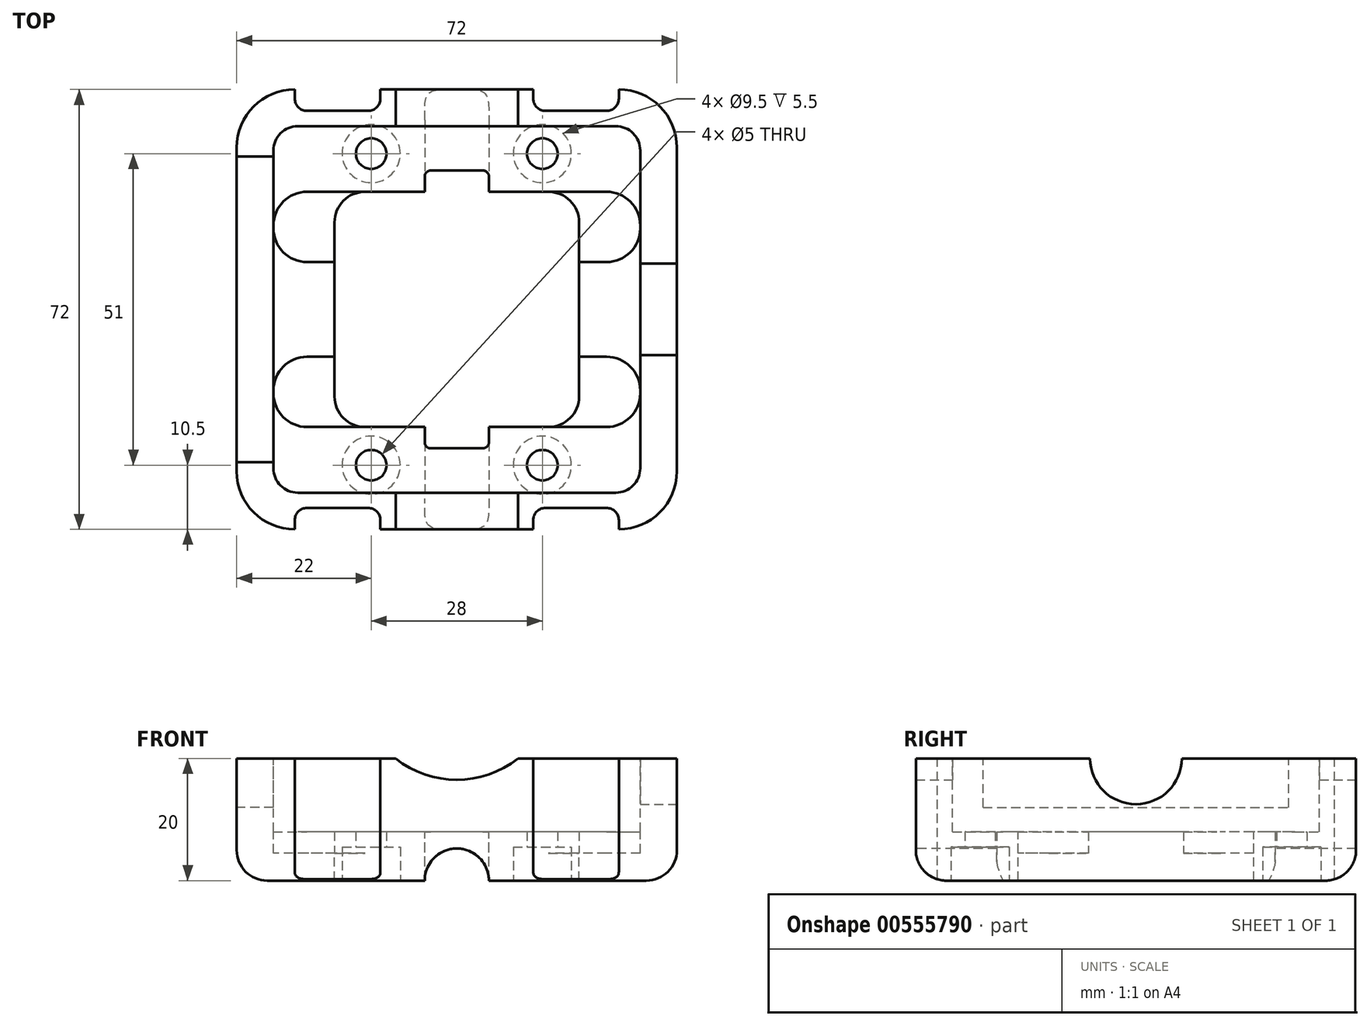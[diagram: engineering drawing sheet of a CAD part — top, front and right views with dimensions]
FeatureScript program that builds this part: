
annotation { "Feature Type Name" : "Feature", "Feature Type Description" : "" }
export const myFeature = defineFeature(function(context is Context, id is Id, definition is map)
    precondition{}
    {
        {
            var Q0;
            Q0=qCreatedBy(makeId("Top.planeOp"),FACE);
            var sketch = newSketch(context, id + "F0", { "sketchPlane" : qUnion([Q0])});
            skLineSegment(sketch, "E0.bottom", {"start": v(36, 36) * mm, "end": v(-36, 36) * mm});
            skLineSegment(sketch, "E0.top", {"start": v(36, -36) * mm, "end": v(-36, -36) * mm});
            skLineSegment(sketch, "E0.left", {"start": v(36, 36) * mm, "end": v(36, -36) * mm});
            skLineSegment(sketch, "E0.right", {"start": v(-36, 36) * mm, "end": v(-36, -36) * mm});
            skPoint(sketch, "E0.middle", {"position": v(0, 0) * mm});
            skSolve(sketch);
        }
        {
            var Q0;
            Q0=makeQuery(id+"F0.imprint","IMPRINT",FACE,{"disambiguationData":[TD([[makeQuery(id+"F0.imprint","IMPRINT",EDGE,{"derivedFrom":sQuery(id+"F0.wireOp",EDGE,"E0.bottom")}),1.0]])]});
            extrude(context, id + "F1", {"entities" : qUnion([Q0]), "depth" : 20 * mm, "offsetDistance" : 25.4 * mm});
        }
        {
            var Q0;
            Q0=makeQuery(id+"F1.opExtrude","CAP_FACE",FACE,{"disambiguationData":[OSD([sQuery(id+"F0.wireOp",EDGE,"E0.bottom"),sQuery(id+"F0.wireOp",EDGE,"E0.top"),sQuery(id+"F0.wireOp",EDGE,"E0.left"),sQuery(id+"F0.wireOp",EDGE,"E0.right")])],"isStart":false});
            var sketch = newSketch(context, id + "F2", { "sketchPlane" : qUnion([Q0])});
            skLineSegment(sketch, "E1.bottom", {"start": v(30, 30) * mm, "end": v(-30, 30) * mm});
            skLineSegment(sketch, "E1.top", {"start": v(30, -30) * mm, "end": v(-30, -30) * mm});
            skLineSegment(sketch, "E1.left", {"start": v(30, 30) * mm, "end": v(30, -30) * mm});
            skLineSegment(sketch, "E1.right", {"start": v(-30, 30) * mm, "end": v(-30, -30) * mm});
            skPoint(sketch, "E1.middle", {"position": v(0, 0) * mm});
            skSolve(sketch);
        }
        {
            var Q0;
            Q0 = qSketchRegion(id + "F2", true);
            extrude(context, id + "F3", {"entities" : qUnion([Q0]), "operationType" : NewBodyOperationType.REMOVE, "oppositeDirection" : true, "depth" : 12 * mm, "offsetDistance" : 25 * mm});
        }
        {
            var Q0;
            Q0=makeQuery(id+"F3.boolean.opBoolean","COPY",FACE,{"derivedFrom":makeQuery(id+"F3.opExtrude","CAP_FACE",FACE,{"disambiguationData":[OSD([sQuery(id+"F2.wireOp",EDGE,"E1.bottom"),sQuery(id+"F2.wireOp",EDGE,"E1.top"),sQuery(id+"F2.wireOp",EDGE,"E1.left"),sQuery(id+"F2.wireOp",EDGE,"E1.right")])],"isStart":false})});
            var sketch = newSketch(context, id + "F4", { "sketchPlane" : qUnion([Q0])});
            skLineSegment(sketch, "E2.bottom", {"start": v(20, 19.25) * mm, "end": v(-20, 19.25) * mm});
            skLineSegment(sketch, "E2.top", {"start": v(20, -19.25) * mm, "end": v(-20, -19.25) * mm});
            skLineSegment(sketch, "E2.left", {"start": v(20, 19.25) * mm, "end": v(20, -19.25) * mm});
            skLineSegment(sketch, "E2.right", {"start": v(-20, 19.25) * mm, "end": v(-20, -19.25) * mm});
            skPoint(sketch, "E2.middle", {"position": v(0, 0) * mm});
            skSolve(sketch);
        }
        {
            var Q0;
            Q0 = qSketchRegion(id + "F4", true);
            extrude(context, id + "F5", {"entities" : qUnion([Q0]), "operationType" : NewBodyOperationType.REMOVE, "endBound" : BoundingType.UP_TO_NEXT, "oppositeDirection" : true, "depth" : 25 * mm, "offsetDistance" : 25 * mm});
        }
        {
            var Q0;
            Q0=makeQuery(id+"F1.opExtrude","SWEPT_FACE",FACE,{"disambiguationData":[OSD([sQuery(id+"F0.wireOp",EDGE,"E0.top")])]});
            var sketch = newSketch(context, id + "F6", { "sketchPlane" : qUnion([Q0])});
            skCircle(sketch, "E3", {"center": v(0, 0) * mm, "radius": 5.25 * mm});
            skSolve(sketch);
        }
        {
            var Q0;
            Q0 = qSketchRegion(id + "F6", true);
            var Q1;
            Q1=makeQuery(id+"F1.opExtrude","SWEPT_FACE",FACE,{"disambiguationData":[OSD([sQuery(id+"F0.wireOp",EDGE,"E0.bottom")])]});
            extrude(context, id + "F7", {"entities" : qUnion([Q0]), "operationType" : NewBodyOperationType.REMOVE, "endBound" : BoundingType.UP_TO_SURFACE, "oppositeDirection" : true, "depth" : 25 * mm, "endBoundEntityFace" : qUnion([Q1]), "offsetDistance" : 25 * mm});
        }
        {
            var Q0;
            Q0=makeQuery(id+"F1.opExtrude","SWEPT_FACE",FACE,{"disambiguationData":[OSD([sQuery(id+"F0.wireOp",EDGE,"E0.right")])]});
            var sketch = newSketch(context, id + "F8", { "sketchPlane" : qUnion([Q0])});
            skLineSegment(sketch, "E4.bottom", {"start": v(25, 12) * mm, "end": v(-25, 12) * mm});
            skLineSegment(sketch, "E4.top", {"start": v(25, 28) * mm, "end": v(-25, 28) * mm});
            skLineSegment(sketch, "E4.left", {"start": v(25, 12) * mm, "end": v(25, 28) * mm});
            skLineSegment(sketch, "E4.right", {"start": v(-25, 12) * mm, "end": v(-25, 28) * mm});
            skPoint(sketch, "E4.middle", {"position": v(0, 20) * mm});
            skSolve(sketch);
        }
        {
            var Q0;
            Q0 = qSketchRegion(id + "F8", true);
            extrude(context, id + "F9", {"entities" : qUnion([Q0]), "operationType" : NewBodyOperationType.REMOVE, "oppositeDirection" : true, "depth" : 6.5 * mm, "offsetDistance" : 25 * mm});
        }
        {
            var Q0;
            Q0=makeQuery(id+"F1.opExtrude","SWEPT_FACE",FACE,{"disambiguationData":[OSD([sQuery(id+"F0.wireOp",EDGE,"E0.left")])]});
            var sketch = newSketch(context, id + "F10", { "sketchPlane" : qUnion([Q0])});
            skCircle(sketch, "E5", {"center": v(0, 20) * mm, "radius": 7.5 * mm});
            skSolve(sketch);
        }
        {
            var Q0;
            Q0 = qSketchRegion(id + "F10", true);
            extrude(context, id + "F11", {"entities" : qUnion([Q0]), "operationType" : NewBodyOperationType.REMOVE, "oppositeDirection" : true, "depth" : 6.5 * mm, "offsetDistance" : 25 * mm});
        }
        {
            var Q0;
            Q0=makeQuery(id+"F3.boolean.opBoolean","COPY",FACE,{"derivedFrom":makeQuery(id+"F3.opExtrude","CAP_FACE",FACE,{"disambiguationData":[OSD([sQuery(id+"F2.wireOp",EDGE,"E1.bottom"),sQuery(id+"F2.wireOp",EDGE,"E1.top"),sQuery(id+"F2.wireOp",EDGE,"E1.left"),sQuery(id+"F2.wireOp",EDGE,"E1.right")])],"isStart":false})});
            var sketch = newSketch(context, id + "F12", { "sketchPlane" : qUnion([Q0])});
            skLineSegment(sketch, "E6.bottom", {"start": v(-5.25, -22.75) * mm, "end": v(5.25, -22.75) * mm});
            skLineSegment(sketch, "E6.top", {"start": v(-5.25, 22.75) * mm, "end": v(5.25, 22.75) * mm});
            skLineSegment(sketch, "E6.left", {"start": v(-5.25, -22.75) * mm, "end": v(-5.25, 22.75) * mm});
            skLineSegment(sketch, "E6.right", {"start": v(5.25, -22.75) * mm, "end": v(5.25, 22.75) * mm});
            skPoint(sketch, "E6.middle", {"position": v(0, 0) * mm});
            skSolve(sketch);
        }
        {
            var Q0;
            Q0 = qSketchRegion(id + "F12", true);
            extrude(context, id + "F13", {"entities" : qUnion([Q0]), "operationType" : NewBodyOperationType.REMOVE, "endBound" : BoundingType.THROUGH_ALL, "depth" : 25 * mm, "offsetDistance" : 25 * mm, "hasSecondDirection" : true, "secondDirectionBound" : SecondDirectionBoundingType.THROUGH_ALL, "secondDirectionOppositeDirection" : true, "secondDirectionDepth" : 25 * mm});
        }
        {
            var Q0;
            Q0=makeQuery(id+"F3.boolean.opBoolean","COPY",FACE,{"derivedFrom":makeQuery(id+"F3.opExtrude","CAP_FACE",FACE,{"disambiguationData":[OSD([sQuery(id+"F2.wireOp",EDGE,"E1.bottom"),sQuery(id+"F2.wireOp",EDGE,"E1.top"),sQuery(id+"F2.wireOp",EDGE,"E1.left"),sQuery(id+"F2.wireOp",EDGE,"E1.right")])],"isStart":false})});
            var sketch = newSketch(context, id + "F14", { "sketchPlane" : qUnion([Q0])});
            skLineSegment(sketch, "E7.bottom", {"start": v(30, 19.25) * mm, "end": v(-30, 19.25) * mm});
            skLineSegment(sketch, "E7.top", {"start": v(30, 7.75) * mm, "end": v(-30, 7.75) * mm});
            skLineSegment(sketch, "E7.left", {"start": v(30, 19.25) * mm, "end": v(30, 7.75) * mm});
            skLineSegment(sketch, "E7.right", {"start": v(-30, 19.25) * mm, "end": v(-30, 7.75) * mm});
            skLineSegment(sketch, "E8.MirrorCS", {"start": v(30, -7.75) * mm, "end": v(-30, -7.75) * mm});
            skLineSegment(sketch, "E9.MirrorCS", {"start": v(30, -19.25) * mm, "end": v(30, -7.75) * mm});
            skLineSegment(sketch, "E10.MirrorCS", {"start": v(30, -19.25) * mm, "end": v(-30, -19.25) * mm});
            skLineSegment(sketch, "E11.MirrorCS", {"start": v(-30, -19.25) * mm, "end": v(-30, -7.75) * mm});
            skSolve(sketch);
        }
        {
            var Q0;
            Q0 = qSketchRegion(id + "F14", true);
            extrude(context, id + "F15", {"entities" : qUnion([Q0]), "operationType" : NewBodyOperationType.REMOVE, "oppositeDirection" : true, "depth" : 3.5 * mm, "offsetDistance" : 25 * mm});
        }
        {
            var Q0;
            {var subQ0=sQuery(id+"F0.wireOp",EDGE,"E0.right");var subQ1=sQuery(id+"F0.wireOp",EDGE,"E0.left");var subQ2=sQuery(id+"F0.wireOp",EDGE,"E0.bottom");Q0=makeQuery(id+"F11.boolean.opBoolean","SPLIT",FACE,{"disambiguationData":[TD([makeQuery(id+"F1.opExtrude","SWEPT_FACE",FACE,{"disambiguationData":[OSD([subQ2])]})])],"derivedFrom":makeQuery(id+"F1.opExtrude","CAP_FACE",FACE,{"disambiguationData":[OSD([subQ2,sQuery(id+"F0.wireOp",EDGE,"E0.top"),subQ1,subQ0])],"isStart":false})});}
            var sketch = newSketch(context, id + "F16", { "sketchPlane" : qUnion([Q0])});
            skLineSegment(sketch, "E12.bottom", {"start": v(-26.5, 32.5) * mm, "end": v(-12.5, 32.5) * mm});
            skLineSegment(sketch, "E12.top", {"start": v(-26.5, 39.5) * mm, "end": v(-12.5, 39.5) * mm});
            skLineSegment(sketch, "E12.left", {"start": v(-26.5, 32.5) * mm, "end": v(-26.5, 39.5) * mm});
            skLineSegment(sketch, "E12.right", {"start": v(-12.5, 32.5) * mm, "end": v(-12.5, 39.5) * mm});
            skPoint(sketch, "E12.middle", {"position": v(-19.5, 36) * mm});
            skLineSegment(sketch, "E13.MirrorCS", {"start": v(-26.5, -32.5) * mm, "end": v(-26.5, -39.5) * mm});
            skLineSegment(sketch, "E14.MirrorCS", {"start": v(-26.5, -32.5) * mm, "end": v(-12.5, -32.5) * mm});
            skLineSegment(sketch, "E15.MirrorCS", {"start": v(-12.5, -32.5) * mm, "end": v(-12.5, -39.5) * mm});
            skLineSegment(sketch, "E16.MirrorCS", {"start": v(-26.5, -39.5) * mm, "end": v(-12.5, -39.5) * mm});
            skLineSegment(sketch, "E17.MirrorCS", {"start": v(26.5, -39.5) * mm, "end": v(12.5, -39.5) * mm});
            skLineSegment(sketch, "E18.MirrorCS", {"start": v(26.5, -32.5) * mm, "end": v(26.5, -39.5) * mm});
            skLineSegment(sketch, "E19.MirrorCS", {"start": v(26.5, -32.5) * mm, "end": v(12.5, -32.5) * mm});
            skLineSegment(sketch, "E20.MirrorCS", {"start": v(12.5, -32.5) * mm, "end": v(12.5, -39.5) * mm});
            skLineSegment(sketch, "E21.MirrorCS", {"start": v(26.5, 32.5) * mm, "end": v(12.5, 32.5) * mm});
            skLineSegment(sketch, "E22.MirrorCS", {"start": v(26.5, 32.5) * mm, "end": v(26.5, 39.5) * mm});
            skLineSegment(sketch, "E23.MirrorCS", {"start": v(26.5, 39.5) * mm, "end": v(12.5, 39.5) * mm});
            skLineSegment(sketch, "E24.MirrorCS", {"start": v(12.5, 32.5) * mm, "end": v(12.5, 39.5) * mm});
            skSolve(sketch);
        }
        {
            var Q0;
            Q0 = qSketchRegion(id + "F16", true);
            extrude(context, id + "F17", {"entities" : qUnion([Q0]), "operationType" : NewBodyOperationType.REMOVE, "endBound" : BoundingType.THROUGH_ALL, "oppositeDirection" : true, "depth" : 25 * mm, "offsetDistance" : 25 * mm});
        }
        {
            var Q0;
            {var subQ0=sQuery(id+"F0.wireOp",EDGE,"E0.bottom");var subQ1=makeQuery(id+"F1.opExtrude","SWEPT_FACE",FACE,{"disambiguationData":[OSD([subQ0])]});Q0=makeQuery(id+"F17.boolean.opBoolean","SPLIT",FACE,{"disambiguationData":[TD([makeQuery(id+"F17.opExtrude","SWEPT_FACE",FACE,{"disambiguationData":[OSD([sQuery(id+"F16.wireOp",EDGE,"E12.right")])]})])],"derivedFrom":subQ1});}
            var sketch = newSketch(context, id + "F18", { "sketchPlane" : qUnion([Q0])});
            skArc(sketch, "E25", {"start": v(-10, 20) * mm, "mid": v(0, 16.5) * mm, "end": v(10, 20) * mm});
            skLineSegment(sketch, "E26", {"start": v(-10, 20) * mm, "end": v(10, 20) * mm});
            skSolve(sketch);
        }
        {
            var Q0;
            Q0 = qSketchRegion(id + "F18", true);
            extrude(context, id + "F19", {"entities" : qUnion([Q0]), "operationType" : NewBodyOperationType.REMOVE, "endBound" : BoundingType.THROUGH_ALL, "oppositeDirection" : true, "depth" : 25 * mm, "offsetDistance" : 25 * mm});
        }
        {
            var Q0;
            {var subQ0=sQuery(id+"F0.wireOp",EDGE,"E0.left");var subQ1=sQuery(id+"F0.wireOp",EDGE,"E0.top");var subQ2=sQuery(id+"F0.wireOp",EDGE,"E0.bottom");Q0=makeQuery(id+"F7.boolean.opBoolean","SPLIT",FACE,{"disambiguationData":[TD([makeQuery(id+"F1.opExtrude","SWEPT_FACE",FACE,{"disambiguationData":[OSD([subQ0])]})])],"derivedFrom":makeQuery(id+"F1.opExtrude","CAP_FACE",FACE,{"disambiguationData":[OSD([subQ2,subQ1,subQ0,sQuery(id+"F0.wireOp",EDGE,"E0.right")])],"isStart":true})});}
            var sketch = newSketch(context, id + "F20", { "sketchPlane" : qUnion([Q0])});
            skCircle(sketch, "E27", {"center": v(14, -25.5) * mm, "radius": 2.5 * mm});
            skCircle(sketch, "E28.MirrorC", {"center": v(-14, -25.5) * mm, "radius": 2.5 * mm});
            skCircle(sketch, "E29.MirrorC", {"center": v(14, 25.5) * mm, "radius": 2.5 * mm});
            skCircle(sketch, "E30.MirrorC", {"center": v(-14, 25.5) * mm, "radius": 2.5 * mm});
            skCircle(sketch, "E31", {"center": v(14, -25.5) * mm, "radius": 4.75 * mm});
            skCircle(sketch, "E32.MirrorC", {"center": v(-14, -25.5) * mm, "radius": 4.75 * mm});
            skCircle(sketch, "E33.MirrorC", {"center": v(14, 25.5) * mm, "radius": 4.75 * mm});
            skCircle(sketch, "E34.MirrorC", {"center": v(-14, 25.5) * mm, "radius": 4.75 * mm});
            skSolve(sketch);
        }
        {
            var Q0;
            Q0=makeQuery(id+"F1.opExtrude","CAP_EDGE",EDGE,{"disambiguationData":[OSD([sQuery(id+"F0.wireOp",EDGE,"E0.left")])],"isStart":true});
            var Q1;
            {var subQ0=sQuery(id+"F0.wireOp",EDGE,"E0.left");var subQ1=sQuery(id+"F0.wireOp",EDGE,"E0.top");var subQ4=makeQuery(id+"F1.opExtrude","SWEPT_FACE",FACE,{"disambiguationData":[OSD([subQ0])]});Q1=makeQuery(id+"F17.boolean.opBoolean","SPLIT",EDGE,{"disambiguationData":[TD([subQ4])],"derivedFrom":makeQuery(id+"F7.boolean.opBoolean","SPLIT",EDGE,{"disambiguationData":[TD([subQ4])],"derivedFrom":makeQuery(id+"F1.opExtrude","CAP_EDGE",EDGE,{"disambiguationData":[OSD([subQ1])],"isStart":true})})});}
            var Q2;
            {var subQ0=sQuery(id+"F0.wireOp",EDGE,"E0.right");var subQ1=sQuery(id+"F0.wireOp",EDGE,"E0.top");Q2=makeQuery(id+"F17.boolean.opBoolean","SPLIT",EDGE,{"disambiguationData":[TD([makeQuery(id+"F17.opExtrude","SWEPT_FACE",FACE,{"disambiguationData":[OSD([sQuery(id+"F16.wireOp",EDGE,"E15.MirrorCS")])]})])],"derivedFrom":makeQuery(id+"F7.boolean.opBoolean","SPLIT",EDGE,{"disambiguationData":[TD([makeQuery(id+"F1.opExtrude","SWEPT_FACE",FACE,{"disambiguationData":[OSD([subQ0])]})])],"derivedFrom":makeQuery(id+"F1.opExtrude","CAP_EDGE",EDGE,{"disambiguationData":[OSD([subQ1])],"isStart":true})})});}
            var Q3;
            Q3=makeQuery(id+"F1.opExtrude","CAP_EDGE",EDGE,{"disambiguationData":[OSD([sQuery(id+"F0.wireOp",EDGE,"E0.right")])],"isStart":true});
            var Q4;
            {var subQ0=sQuery(id+"F0.wireOp",EDGE,"E0.bottom");var subQ2=sQuery(id+"F0.wireOp",EDGE,"E0.right");var subQ3=makeQuery(id+"F1.opExtrude","SWEPT_FACE",FACE,{"disambiguationData":[OSD([subQ2])]});Q4=makeQuery(id+"F17.boolean.opBoolean","SPLIT",EDGE,{"disambiguationData":[TD([subQ3])],"derivedFrom":makeQuery(id+"F7.boolean.opBoolean","SPLIT",EDGE,{"disambiguationData":[TD([subQ3])],"derivedFrom":makeQuery(id+"F1.opExtrude","CAP_EDGE",EDGE,{"disambiguationData":[OSD([subQ0])],"isStart":true})})});}
            var Q5;
            {var subQ0=sQuery(id+"F0.wireOp",EDGE,"E0.bottom");var subQ2=sQuery(id+"F0.wireOp",EDGE,"E0.left");Q5=makeQuery(id+"F17.boolean.opBoolean","SPLIT",EDGE,{"disambiguationData":[TD([makeQuery(id+"F17.opExtrude","SWEPT_FACE",FACE,{"disambiguationData":[OSD([sQuery(id+"F16.wireOp",EDGE,"E24.MirrorCS")])]})])],"derivedFrom":makeQuery(id+"F7.boolean.opBoolean","SPLIT",EDGE,{"disambiguationData":[TD([makeQuery(id+"F1.opExtrude","SWEPT_FACE",FACE,{"disambiguationData":[OSD([subQ2])]})])],"derivedFrom":makeQuery(id+"F1.opExtrude","CAP_EDGE",EDGE,{"disambiguationData":[OSD([subQ0])],"isStart":true})})});}
            var Q6;
            Q6=makeQuery(id+"F5.boolean.opBoolean","COPY",EDGE,{"derivedFrom":makeQuery(id+"F5.opExtrude","SWEPT_EDGE",EDGE,{"disambiguationData":[OSD([sQuery(id+"F4.wireOp",EDGE,"E2.bottom"),sQuery(id+"F4.wireOp",EDGE,"E2.left")])]})});
            var Q7;
            Q7=makeQuery(id+"F5.boolean.opBoolean","COPY",EDGE,{"derivedFrom":makeQuery(id+"F5.opExtrude","SWEPT_EDGE",EDGE,{"disambiguationData":[OSD([sQuery(id+"F4.wireOp",EDGE,"E2.bottom"),sQuery(id+"F4.wireOp",EDGE,"E2.right")])]})});
            var Q8;
            Q8=makeQuery(id+"F5.boolean.opBoolean","COPY",EDGE,{"derivedFrom":makeQuery(id+"F5.opExtrude","SWEPT_EDGE",EDGE,{"disambiguationData":[OSD([sQuery(id+"F4.wireOp",EDGE,"E2.top"),sQuery(id+"F4.wireOp",EDGE,"E2.right")])]})});
            var Q9;
            Q9=makeQuery(id+"F5.boolean.opBoolean","COPY",EDGE,{"derivedFrom":makeQuery(id+"F5.opExtrude","SWEPT_EDGE",EDGE,{"disambiguationData":[OSD([sQuery(id+"F4.wireOp",EDGE,"E2.top"),sQuery(id+"F4.wireOp",EDGE,"E2.left")])]})});
            var Q10;
            {var subQ0=sQuery(id+"F0.wireOp",EDGE,"E0.right");var subQ1=sQuery(id+"F0.wireOp",EDGE,"E0.top");var subQ4=makeQuery(id+"F1.opExtrude","SWEPT_FACE",FACE,{"disambiguationData":[OSD([subQ0])]});Q10=makeQuery(id+"F17.boolean.opBoolean","SPLIT",EDGE,{"disambiguationData":[TD([subQ4])],"derivedFrom":makeQuery(id+"F7.boolean.opBoolean","SPLIT",EDGE,{"disambiguationData":[TD([subQ4])],"derivedFrom":makeQuery(id+"F1.opExtrude","CAP_EDGE",EDGE,{"disambiguationData":[OSD([subQ1])],"isStart":true})})});}
            var Q11;
            {var subQ0=sQuery(id+"F0.wireOp",EDGE,"E0.bottom");var subQ2=sQuery(id+"F0.wireOp",EDGE,"E0.left");var subQ4=makeQuery(id+"F1.opExtrude","SWEPT_FACE",FACE,{"disambiguationData":[OSD([subQ2])]});Q11=makeQuery(id+"F17.boolean.opBoolean","SPLIT",EDGE,{"disambiguationData":[TD([subQ4])],"derivedFrom":makeQuery(id+"F7.boolean.opBoolean","SPLIT",EDGE,{"disambiguationData":[TD([subQ4])],"derivedFrom":makeQuery(id+"F1.opExtrude","CAP_EDGE",EDGE,{"disambiguationData":[OSD([subQ0])],"isStart":true})})});}
            fillet(context, id + "F21", {"entities" : qUnion([Q0, Q1, Q2, Q3, Q4, Q5, Q6, Q7, Q8, Q9, Q10, Q11]), "radius" : 5 * mm, "tangentPropagation" : true, "allowEdgeOverflow" : false});
        }
        {
            var Q0;
            Q0=makeQuery(id+"F17.boolean.opBoolean","COPY",EDGE,{"derivedFrom":makeQuery(id+"F17.opExtrude","SWEPT_EDGE",EDGE,{"disambiguationData":[OSD([sQuery(id+"F16.wireOp",EDGE,"E21.MirrorCS"),sQuery(id+"F16.wireOp",EDGE,"E24.MirrorCS")])]})});
            var Q1;
            Q1=makeQuery(id+"F17.boolean.opBoolean","COPY",EDGE,{"derivedFrom":makeQuery(id+"F17.opExtrude","SWEPT_EDGE",EDGE,{"disambiguationData":[OSD([sQuery(id+"F16.wireOp",EDGE,"E12.bottom"),sQuery(id+"F16.wireOp",EDGE,"E12.left")])]})});
            var Q2;
            Q2=makeQuery(id+"F17.boolean.opBoolean","COPY",EDGE,{"derivedFrom":makeQuery(id+"F17.opExtrude","SWEPT_EDGE",EDGE,{"disambiguationData":[OSD([sQuery(id+"F16.wireOp",EDGE,"E12.bottom"),sQuery(id+"F16.wireOp",EDGE,"E12.right")])]})});
            var Q3;
            Q3=makeQuery(id+"F17.boolean.opBoolean","COPY",EDGE,{"derivedFrom":makeQuery(id+"F17.opExtrude","SWEPT_EDGE",EDGE,{"disambiguationData":[OSD([sQuery(id+"F16.wireOp",EDGE,"E21.MirrorCS"),sQuery(id+"F16.wireOp",EDGE,"E22.MirrorCS")])]})});
            var Q4;
            Q4=makeQuery(id+"F17.boolean.opBoolean","COPY",EDGE,{"derivedFrom":makeQuery(id+"F17.opExtrude","SWEPT_EDGE",EDGE,{"disambiguationData":[OSD([sQuery(id+"F16.wireOp",EDGE,"E13.MirrorCS"),sQuery(id+"F16.wireOp",EDGE,"E14.MirrorCS")])]})});
            var Q5;
            Q5=makeQuery(id+"F17.boolean.opBoolean","COPY",EDGE,{"derivedFrom":makeQuery(id+"F17.opExtrude","SWEPT_EDGE",EDGE,{"disambiguationData":[OSD([sQuery(id+"F16.wireOp",EDGE,"E19.MirrorCS"),sQuery(id+"F16.wireOp",EDGE,"E20.MirrorCS")])]})});
            var Q6;
            Q6=makeQuery(id+"F17.boolean.opBoolean","COPY",EDGE,{"derivedFrom":makeQuery(id+"F17.opExtrude","SWEPT_EDGE",EDGE,{"disambiguationData":[OSD([sQuery(id+"F16.wireOp",EDGE,"E14.MirrorCS"),sQuery(id+"F16.wireOp",EDGE,"E15.MirrorCS")])]})});
            var Q7;
            Q7=makeQuery(id+"F17.boolean.opBoolean","COPY",EDGE,{"derivedFrom":makeQuery(id+"F17.opExtrude","SWEPT_EDGE",EDGE,{"disambiguationData":[OSD([sQuery(id+"F16.wireOp",EDGE,"E18.MirrorCS"),sQuery(id+"F16.wireOp",EDGE,"E19.MirrorCS")])]})});
            fillet(context, id + "F22", {"entities" : qUnion([Q0, Q1, Q2, Q3, Q4, Q5, Q6, Q7]), "radius" : 2 * mm, "tangentPropagation" : true, "allowEdgeOverflow" : false});
        }
        {
            var Q0;
            Q0=makeQuery(id+"F15.boolean.opBoolean","COPY",EDGE,{"derivedFrom":makeQuery(id+"F15.opExtrude","SWEPT_EDGE",EDGE,{"disambiguationData":[OSD([sQuery(id+"F2.wireOp",EDGE,"E1.right"),sQuery(id+"F14.wireOp",EDGE,"E7.bottom"),sQuery(id+"F14.wireOp",EDGE,"E7.right")])]})});
            var Q1;
            Q1=makeQuery(id+"F15.boolean.opBoolean","COPY",EDGE,{"derivedFrom":makeQuery(id+"F15.opExtrude","SWEPT_EDGE",EDGE,{"disambiguationData":[OSD([sQuery(id+"F2.wireOp",EDGE,"E1.right"),sQuery(id+"F14.wireOp",EDGE,"E7.top"),sQuery(id+"F14.wireOp",EDGE,"E7.right")])]})});
            var Q2;
            Q2=makeQuery(id+"F15.boolean.opBoolean","COPY",EDGE,{"derivedFrom":makeQuery(id+"F15.opExtrude","SWEPT_EDGE",EDGE,{"disambiguationData":[OSD([sQuery(id+"F2.wireOp",EDGE,"E1.right"),sQuery(id+"F14.wireOp",EDGE,"E10.MirrorCS"),sQuery(id+"F14.wireOp",EDGE,"E11.MirrorCS")])]})});
            var Q3;
            Q3=makeQuery(id+"F15.boolean.opBoolean","COPY",EDGE,{"derivedFrom":makeQuery(id+"F15.opExtrude","SWEPT_EDGE",EDGE,{"disambiguationData":[OSD([sQuery(id+"F2.wireOp",EDGE,"E1.right"),sQuery(id+"F14.wireOp",EDGE,"E8.MirrorCS"),sQuery(id+"F14.wireOp",EDGE,"E11.MirrorCS")])]})});
            var Q4;
            Q4=makeQuery(id+"F15.boolean.opBoolean","COPY",EDGE,{"derivedFrom":makeQuery(id+"F15.opExtrude","SWEPT_EDGE",EDGE,{"disambiguationData":[OSD([sQuery(id+"F2.wireOp",EDGE,"E1.left"),sQuery(id+"F14.wireOp",EDGE,"E9.MirrorCS"),sQuery(id+"F14.wireOp",EDGE,"E10.MirrorCS")])]})});
            var Q5;
            Q5=makeQuery(id+"F15.boolean.opBoolean","COPY",EDGE,{"derivedFrom":makeQuery(id+"F15.opExtrude","SWEPT_EDGE",EDGE,{"disambiguationData":[OSD([sQuery(id+"F2.wireOp",EDGE,"E1.left"),sQuery(id+"F14.wireOp",EDGE,"E8.MirrorCS"),sQuery(id+"F14.wireOp",EDGE,"E9.MirrorCS")])]})});
            var Q6;
            Q6=makeQuery(id+"F15.boolean.opBoolean","COPY",EDGE,{"derivedFrom":makeQuery(id+"F15.opExtrude","SWEPT_EDGE",EDGE,{"disambiguationData":[OSD([sQuery(id+"F2.wireOp",EDGE,"E1.left"),sQuery(id+"F14.wireOp",EDGE,"E7.bottom"),sQuery(id+"F14.wireOp",EDGE,"E7.left")])]})});
            var Q7;
            Q7=makeQuery(id+"F15.boolean.opBoolean","COPY",EDGE,{"derivedFrom":makeQuery(id+"F15.opExtrude","SWEPT_EDGE",EDGE,{"disambiguationData":[OSD([sQuery(id+"F2.wireOp",EDGE,"E1.left"),sQuery(id+"F14.wireOp",EDGE,"E7.top"),sQuery(id+"F14.wireOp",EDGE,"E7.left")])]})});
            fillet(context, id + "F23", {"entities" : qUnion([Q0, Q1, Q2, Q3, Q4, Q5, Q6, Q7]), "radius" : 5.5 * mm, "tangentPropagation" : true, "allowEdgeOverflow" : false});
        }
        {
            var Q0;
            Q0=makeQuery(id+"F3.boolean.opBoolean","COPY",EDGE,{"derivedFrom":makeQuery(id+"F3.opExtrude","SWEPT_EDGE",EDGE,{"disambiguationData":[OSD([sQuery(id+"F2.wireOp",EDGE,"E1.top"),sQuery(id+"F2.wireOp",EDGE,"E1.right")])]})});
            var Q1;
            Q1=makeQuery(id+"F3.boolean.opBoolean","COPY",EDGE,{"derivedFrom":makeQuery(id+"F3.opExtrude","SWEPT_EDGE",EDGE,{"disambiguationData":[OSD([sQuery(id+"F2.wireOp",EDGE,"E1.bottom"),sQuery(id+"F2.wireOp",EDGE,"E1.right")])]})});
            var Q2;
            Q2=makeQuery(id+"F3.boolean.opBoolean","COPY",EDGE,{"derivedFrom":makeQuery(id+"F3.opExtrude","SWEPT_EDGE",EDGE,{"disambiguationData":[OSD([sQuery(id+"F2.wireOp",EDGE,"E1.bottom"),sQuery(id+"F2.wireOp",EDGE,"E1.left")])]})});
            var Q3;
            Q3=makeQuery(id+"F3.boolean.opBoolean","COPY",EDGE,{"derivedFrom":makeQuery(id+"F3.opExtrude","SWEPT_EDGE",EDGE,{"disambiguationData":[OSD([sQuery(id+"F2.wireOp",EDGE,"E1.top"),sQuery(id+"F2.wireOp",EDGE,"E1.left")])]})});
            fillet(context, id + "F24", {"entities" : qUnion([Q0, Q1, Q2, Q3]), "radius" : 4 * mm, "tangentPropagation" : true, "allowEdgeOverflow" : false});
        }
        {
            var Q0;
            Q0=makeQuery(id+"F13.boolean.opBoolean","COPY",EDGE,{"derivedFrom":makeQuery(id+"F13.opExtrude","SWEPT_EDGE",EDGE,{"disambiguationData":[OSD([sQuery(id+"F12.wireOp",EDGE,"E6.top"),sQuery(id+"F12.wireOp",EDGE,"E6.left")])]})});
            var Q1;
            Q1=makeQuery(id+"F13.boolean.opBoolean","COPY",EDGE,{"derivedFrom":makeQuery(id+"F13.opExtrude","SWEPT_EDGE",EDGE,{"disambiguationData":[OSD([sQuery(id+"F12.wireOp",EDGE,"E6.top"),sQuery(id+"F12.wireOp",EDGE,"E6.right")])]})});
            var Q2;
            Q2=makeQuery(id+"F13.boolean.opBoolean","COPY",EDGE,{"derivedFrom":makeQuery(id+"F13.opExtrude","SWEPT_EDGE",EDGE,{"disambiguationData":[OSD([sQuery(id+"F12.wireOp",EDGE,"E6.bottom"),sQuery(id+"F12.wireOp",EDGE,"E6.right")])]})});
            var Q3;
            Q3=makeQuery(id+"F13.boolean.opBoolean","COPY",EDGE,{"derivedFrom":makeQuery(id+"F13.opExtrude","SWEPT_EDGE",EDGE,{"disambiguationData":[OSD([sQuery(id+"F12.wireOp",EDGE,"E6.bottom"),sQuery(id+"F12.wireOp",EDGE,"E6.left")])]})});
            fillet(context, id + "F25", {"entities" : qUnion([Q0, Q1, Q2, Q3]), "radius" : 1 * mm, "tangentPropagation" : true, "allowEdgeOverflow" : false});
        }
        {
            var Q0;
            Q0 = qSketchRegion(id + "F20", true);
            extrude(context, id + "F26", {"entities" : qUnion([Q0]), "operationType" : NewBodyOperationType.REMOVE, "oppositeDirection" : true, "depth" : 5.5 * mm, "offsetDistance" : 25 * mm});
        }
        {
            var Q0;
            {var subQ0=sQuery(id+"F0.wireOp",EDGE,"E0.left");var subQ1=sQuery(id+"F0.wireOp",EDGE,"E0.top");var subQ2=sQuery(id+"F0.wireOp",EDGE,"E0.bottom");Q0=makeQuery(id+"F26.boolean.opBoolean","SPLIT",FACE,{"disambiguationData":[TD([makeQuery(id+"F26.opExtrude","SWEPT_FACE",FACE,{"disambiguationData":[OSD([sQuery(id+"F20.wireOp",EDGE,"E27")])]})])],"derivedFrom":makeQuery(id+"F7.boolean.opBoolean","SPLIT",FACE,{"disambiguationData":[TD([makeQuery(id+"F1.opExtrude","SWEPT_FACE",FACE,{"disambiguationData":[OSD([subQ0])]})])],"derivedFrom":makeQuery(id+"F1.opExtrude","CAP_FACE",FACE,{"disambiguationData":[OSD([subQ2,subQ1,subQ0,sQuery(id+"F0.wireOp",EDGE,"E0.right")])],"isStart":true})})});}
            var Q1;
            {var subQ0=sQuery(id+"F0.wireOp",EDGE,"E0.top");var subQ1=sQuery(id+"F0.wireOp",EDGE,"E0.right");var subQ2=sQuery(id+"F0.wireOp",EDGE,"E0.bottom");Q1=makeQuery(id+"F26.boolean.opBoolean","SPLIT",FACE,{"disambiguationData":[TD([makeQuery(id+"F26.opExtrude","SWEPT_FACE",FACE,{"disambiguationData":[OSD([sQuery(id+"F20.wireOp",EDGE,"E28.MirrorC")])]})])],"derivedFrom":makeQuery(id+"F7.boolean.opBoolean","SPLIT",FACE,{"disambiguationData":[TD([makeQuery(id+"F1.opExtrude","SWEPT_FACE",FACE,{"disambiguationData":[OSD([subQ1])]})])],"derivedFrom":makeQuery(id+"F1.opExtrude","CAP_FACE",FACE,{"disambiguationData":[OSD([subQ2,subQ0,sQuery(id+"F0.wireOp",EDGE,"E0.left"),subQ1])],"isStart":true})})});}
            var Q2;
            {var subQ0=sQuery(id+"F0.wireOp",EDGE,"E0.top");var subQ1=sQuery(id+"F0.wireOp",EDGE,"E0.right");var subQ2=sQuery(id+"F0.wireOp",EDGE,"E0.bottom");Q2=makeQuery(id+"F26.boolean.opBoolean","SPLIT",FACE,{"disambiguationData":[TD([makeQuery(id+"F26.opExtrude","SWEPT_FACE",FACE,{"disambiguationData":[OSD([sQuery(id+"F20.wireOp",EDGE,"E30.MirrorC")])]})])],"derivedFrom":makeQuery(id+"F7.boolean.opBoolean","SPLIT",FACE,{"disambiguationData":[TD([makeQuery(id+"F1.opExtrude","SWEPT_FACE",FACE,{"disambiguationData":[OSD([subQ1])]})])],"derivedFrom":makeQuery(id+"F1.opExtrude","CAP_FACE",FACE,{"disambiguationData":[OSD([subQ2,subQ0,sQuery(id+"F0.wireOp",EDGE,"E0.left"),subQ1])],"isStart":true})})});}
            var Q3;
            {var subQ0=sQuery(id+"F0.wireOp",EDGE,"E0.left");var subQ1=sQuery(id+"F0.wireOp",EDGE,"E0.top");var subQ2=sQuery(id+"F0.wireOp",EDGE,"E0.bottom");Q3=makeQuery(id+"F26.boolean.opBoolean","SPLIT",FACE,{"disambiguationData":[TD([makeQuery(id+"F26.opExtrude","SWEPT_FACE",FACE,{"disambiguationData":[OSD([sQuery(id+"F20.wireOp",EDGE,"E29.MirrorC")])]})])],"derivedFrom":makeQuery(id+"F7.boolean.opBoolean","SPLIT",FACE,{"disambiguationData":[TD([makeQuery(id+"F1.opExtrude","SWEPT_FACE",FACE,{"disambiguationData":[OSD([subQ0])]})])],"derivedFrom":makeQuery(id+"F1.opExtrude","CAP_FACE",FACE,{"disambiguationData":[OSD([subQ2,subQ1,subQ0,sQuery(id+"F0.wireOp",EDGE,"E0.right")])],"isStart":true})})});}
            extrude(context, id + "F27", {"entities" : qUnion([Q0, Q1, Q2, Q3]), "operationType" : NewBodyOperationType.REMOVE, "endBound" : BoundingType.THROUGH_ALL, "oppositeDirection" : true, "depth" : 25 * mm, "offsetDistance" : 25 * mm});
        }
        {
            var Q0;
            Q0=makeQuery(id+"F1.opExtrude","SWEPT_EDGE",EDGE,{"disambiguationData":[OSD([sQuery(id+"F0.wireOp",EDGE,"E0.top"),sQuery(id+"F0.wireOp",EDGE,"E0.left")])]});
            var Q1;
            Q1=makeQuery(id+"F1.opExtrude","SWEPT_EDGE",EDGE,{"disambiguationData":[OSD([sQuery(id+"F0.wireOp",EDGE,"E0.top"),sQuery(id+"F0.wireOp",EDGE,"E0.right")])]});
            var Q2;
            Q2=makeQuery(id+"F1.opExtrude","SWEPT_EDGE",EDGE,{"disambiguationData":[OSD([sQuery(id+"F0.wireOp",EDGE,"E0.bottom"),sQuery(id+"F0.wireOp",EDGE,"E0.right")])]});
            var Q3;
            Q3=makeQuery(id+"F1.opExtrude","SWEPT_EDGE",EDGE,{"disambiguationData":[OSD([sQuery(id+"F0.wireOp",EDGE,"E0.bottom"),sQuery(id+"F0.wireOp",EDGE,"E0.left")])]});
            fillet(context, id + "F28", {"entities" : qUnion([Q0, Q1, Q2, Q3]), "radius" : 9.5 * mm, "tangentPropagation" : true, "allowEdgeOverflow" : false});
        }
    });
